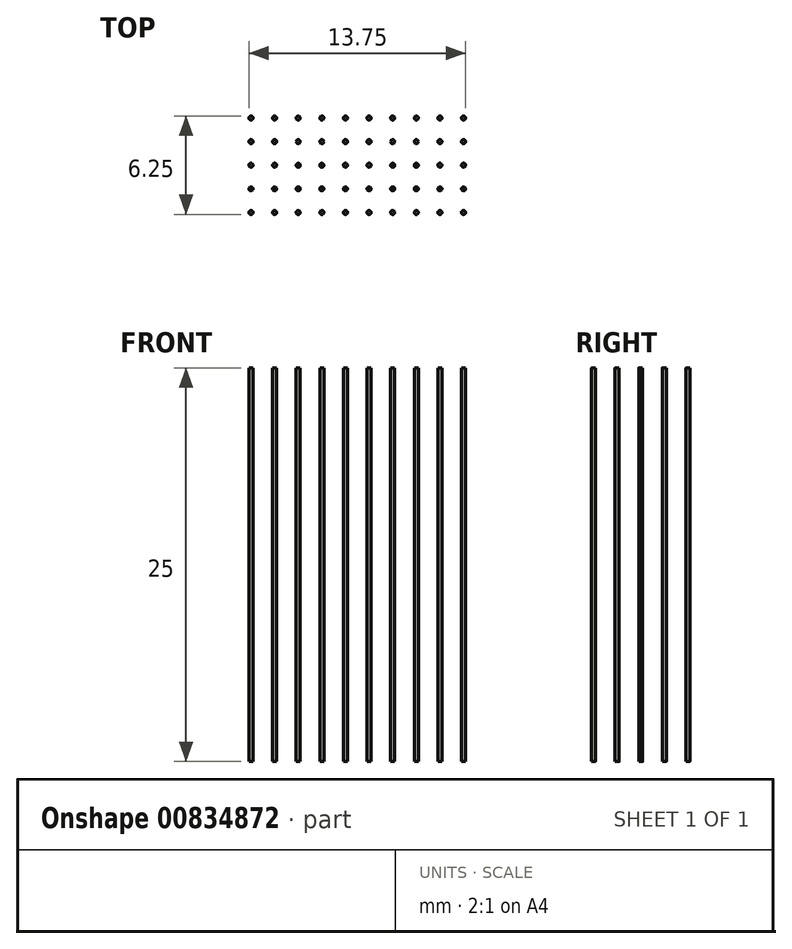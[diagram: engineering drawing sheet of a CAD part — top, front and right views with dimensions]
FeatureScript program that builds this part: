
annotation { "Feature Type Name" : "Feature", "Feature Type Description" : "" }
export const myFeature = defineFeature(function(context is Context, id is Id, definition is map)
    precondition{}
    {
        {
            var Q0;
            Q0=qCreatedBy(makeId("Top.planeOp"),FACE);
            var sketch = newSketch(context, id + "F0", { "sketchPlane" : qUnion([Q0])});
            skCircle(sketch, "E0", {"center": v(-57.44, 51.7) * mm, "radius": 0.13 * mm});
            skCircle(sketch, "E1.0.1.0", {"center": v(-57.44, 50.2) * mm, "radius": 0.13 * mm});
            skCircle(sketch, "E1.0.2.0", {"center": v(-57.44, 48.7) * mm, "radius": 0.13 * mm});
            skCircle(sketch, "E1.0.3.0", {"center": v(-57.44, 47.2) * mm, "radius": 0.13 * mm});
            skCircle(sketch, "E1.0.4.0", {"center": v(-57.44, 45.7) * mm, "radius": 0.13 * mm});
            skCircle(sketch, "E1.1.0.0", {"center": v(-55.94, 51.7) * mm, "radius": 0.13 * mm});
            skCircle(sketch, "E1.1.1.0", {"center": v(-55.94, 50.2) * mm, "radius": 0.13 * mm});
            skCircle(sketch, "E1.1.2.0", {"center": v(-55.94, 48.7) * mm, "radius": 0.13 * mm});
            skCircle(sketch, "E1.1.3.0", {"center": v(-55.94, 47.2) * mm, "radius": 0.13 * mm});
            skCircle(sketch, "E1.1.4.0", {"center": v(-55.94, 45.7) * mm, "radius": 0.13 * mm});
            skCircle(sketch, "E1.2.0.0", {"center": v(-54.44, 51.7) * mm, "radius": 0.13 * mm});
            skCircle(sketch, "E1.2.1.0", {"center": v(-54.44, 50.2) * mm, "radius": 0.13 * mm});
            skCircle(sketch, "E1.2.2.0", {"center": v(-54.44, 48.7) * mm, "radius": 0.13 * mm});
            skCircle(sketch, "E1.2.3.0", {"center": v(-54.44, 47.2) * mm, "radius": 0.13 * mm});
            skCircle(sketch, "E1.2.4.0", {"center": v(-54.44, 45.7) * mm, "radius": 0.13 * mm});
            skCircle(sketch, "E1.3.0.0", {"center": v(-52.94, 51.7) * mm, "radius": 0.13 * mm});
            skCircle(sketch, "E1.3.1.0", {"center": v(-52.94, 50.2) * mm, "radius": 0.13 * mm});
            skCircle(sketch, "E1.3.2.0", {"center": v(-52.94, 48.7) * mm, "radius": 0.13 * mm});
            skCircle(sketch, "E1.3.3.0", {"center": v(-52.94, 47.2) * mm, "radius": 0.13 * mm});
            skCircle(sketch, "E1.3.4.0", {"center": v(-52.94, 45.7) * mm, "radius": 0.13 * mm});
            skCircle(sketch, "E1.4.0.0", {"center": v(-51.44, 51.7) * mm, "radius": 0.13 * mm});
            skCircle(sketch, "E1.4.1.0", {"center": v(-51.44, 50.2) * mm, "radius": 0.13 * mm});
            skCircle(sketch, "E1.4.2.0", {"center": v(-51.44, 48.7) * mm, "radius": 0.13 * mm});
            skCircle(sketch, "E1.4.3.0", {"center": v(-51.44, 47.2) * mm, "radius": 0.13 * mm});
            skCircle(sketch, "E1.4.4.0", {"center": v(-51.44, 45.7) * mm, "radius": 0.13 * mm});
            skCircle(sketch, "E1.5.0.0", {"center": v(-49.94, 51.7) * mm, "radius": 0.13 * mm});
            skCircle(sketch, "E1.5.1.0", {"center": v(-49.94, 50.2) * mm, "radius": 0.13 * mm});
            skCircle(sketch, "E1.5.2.0", {"center": v(-49.94, 48.7) * mm, "radius": 0.13 * mm});
            skCircle(sketch, "E1.5.3.0", {"center": v(-49.94, 47.2) * mm, "radius": 0.13 * mm});
            skCircle(sketch, "E1.5.4.0", {"center": v(-49.94, 45.7) * mm, "radius": 0.13 * mm});
            skCircle(sketch, "E1.6.0.0", {"center": v(-48.44, 51.7) * mm, "radius": 0.13 * mm});
            skCircle(sketch, "E1.6.1.0", {"center": v(-48.44, 50.2) * mm, "radius": 0.13 * mm});
            skCircle(sketch, "E1.6.2.0", {"center": v(-48.44, 48.7) * mm, "radius": 0.13 * mm});
            skCircle(sketch, "E1.6.3.0", {"center": v(-48.44, 47.2) * mm, "radius": 0.13 * mm});
            skCircle(sketch, "E1.6.4.0", {"center": v(-48.44, 45.7) * mm, "radius": 0.13 * mm});
            skCircle(sketch, "E1.7.0.0", {"center": v(-46.94, 51.7) * mm, "radius": 0.13 * mm});
            skCircle(sketch, "E1.7.1.0", {"center": v(-46.94, 50.2) * mm, "radius": 0.13 * mm});
            skCircle(sketch, "E1.7.2.0", {"center": v(-46.94, 48.7) * mm, "radius": 0.13 * mm});
            skCircle(sketch, "E1.7.3.0", {"center": v(-46.94, 47.2) * mm, "radius": 0.13 * mm});
            skCircle(sketch, "E1.7.4.0", {"center": v(-46.94, 45.7) * mm, "radius": 0.13 * mm});
            skCircle(sketch, "E1.8.0.0", {"center": v(-45.44, 51.7) * mm, "radius": 0.13 * mm});
            skCircle(sketch, "E1.8.1.0", {"center": v(-45.44, 50.2) * mm, "radius": 0.13 * mm});
            skCircle(sketch, "E1.8.2.0", {"center": v(-45.44, 48.7) * mm, "radius": 0.13 * mm});
            skCircle(sketch, "E1.8.3.0", {"center": v(-45.44, 47.2) * mm, "radius": 0.13 * mm});
            skCircle(sketch, "E1.8.4.0", {"center": v(-45.44, 45.7) * mm, "radius": 0.13 * mm});
            skCircle(sketch, "E1.9.0.0", {"center": v(-43.94, 51.7) * mm, "radius": 0.13 * mm});
            skCircle(sketch, "E1.9.1.0", {"center": v(-43.94, 50.2) * mm, "radius": 0.13 * mm});
            skCircle(sketch, "E1.9.2.0", {"center": v(-43.94, 48.7) * mm, "radius": 0.13 * mm});
            skCircle(sketch, "E1.9.3.0", {"center": v(-43.94, 47.2) * mm, "radius": 0.13 * mm});
            skCircle(sketch, "E1.9.4.0", {"center": v(-43.94, 45.7) * mm, "radius": 0.13 * mm});
            skLineSegment(sketch, "E1.direction1", {"start": v(-57.44, 51.7) * mm, "end": v(-55.94, 51.7) * mm, "construction": true});
            skLineSegment(sketch, "E1.direction2", {"start": v(-57.44, 51.7) * mm, "end": v(-57.44, 50.2) * mm, "construction": true});
            skSolve(sketch);
        }
        {
            var Q0;
            Q0 = qSketchRegion(id + "F0", true);
            extrude(context, id + "F1", {"entities" : qUnion([Q0]), "oppositeDirection" : true, "depth" : 25 * mm, "offsetDistance" : 25 * mm});
        }
    });
